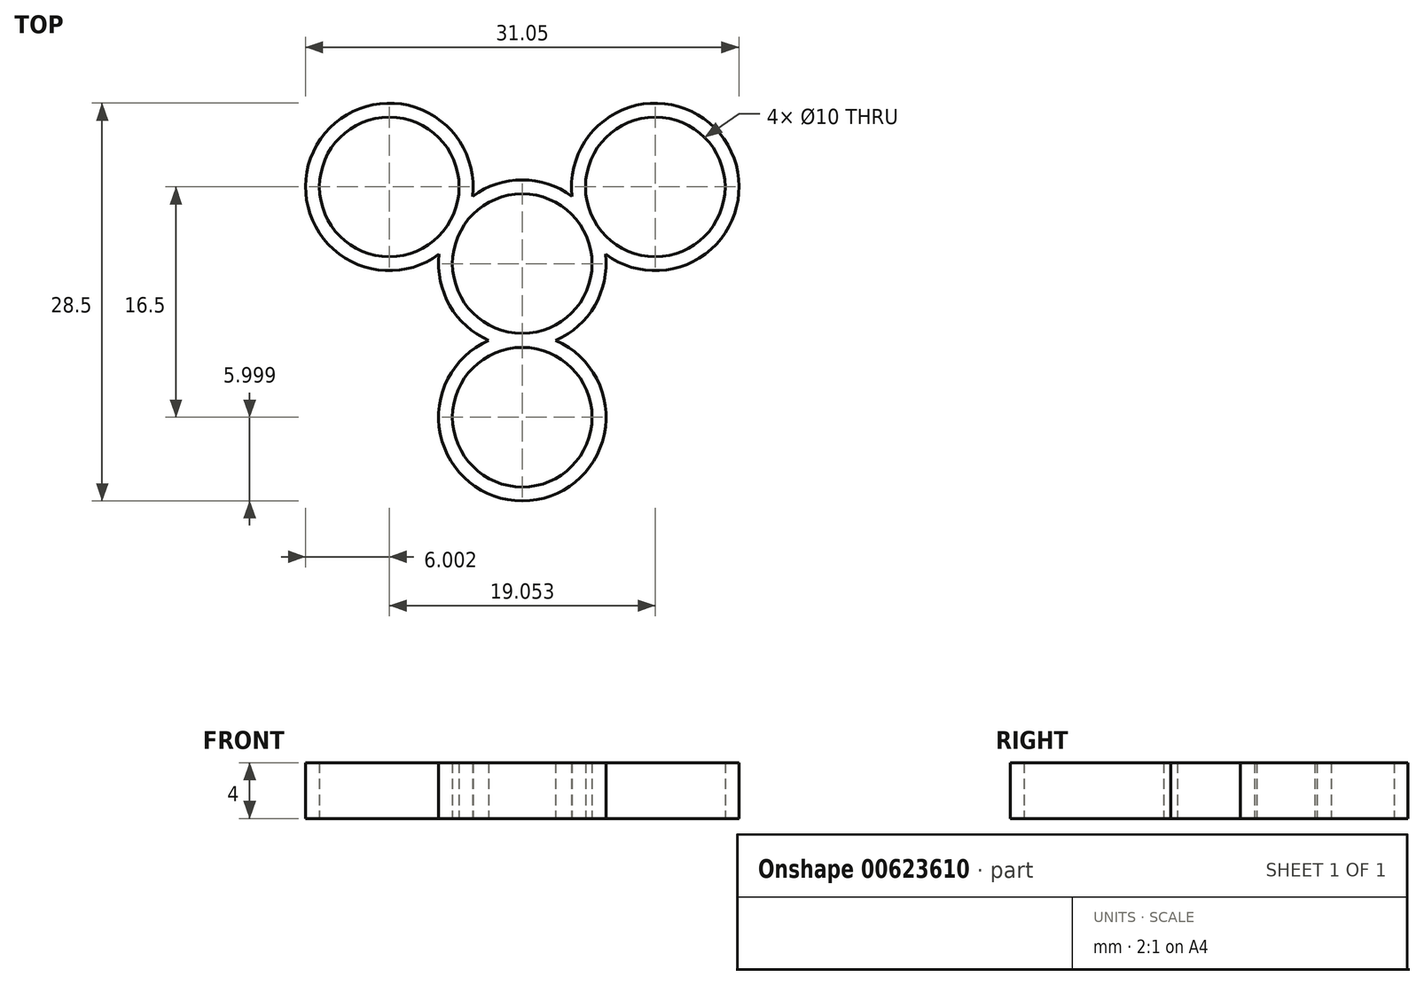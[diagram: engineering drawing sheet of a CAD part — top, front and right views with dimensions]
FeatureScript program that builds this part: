
annotation { "Feature Type Name" : "Feature", "Feature Type Description" : "" }
export const myFeature = defineFeature(function(context is Context, id is Id, definition is map)
    precondition{}
    {
        {
            var Q0;
            Q0=qCreatedBy(makeId("Top.planeOp"),FACE);
            var sketch = newSketch(context, id + "F0", { "sketchPlane" : qUnion([Q0])});
            skCircle(sketch, "E0", {"center": v(-137.71, -10.27) * mm, "radius": 5 * mm});
            skCircle(sketch, "E1", {"center": v(-137.71, -10.27) * mm, "radius": 6 * mm});
            skLineSegment(sketch, "E2", {"start": v(-137.71, -10.27) * mm, "end": v(-137.71, -21.27) * mm});
            skLineSegment(sketch, "E3", {"start": v(-137.71, -10.27) * mm, "end": v(-128.19, -4.77) * mm});
            skLineSegment(sketch, "E4", {"start": v(-137.71, -10.27) * mm, "end": v(-147.24, -4.77) * mm});
            skCircle(sketch, "E5", {"center": v(-128.19, -4.77) * mm, "radius": 5 * mm});
            skCircle(sketch, "E6", {"center": v(-128.19, -4.77) * mm, "radius": 6 * mm});
            skCircle(sketch, "E7", {"center": v(-147.24, -4.77) * mm, "radius": 5 * mm});
            skCircle(sketch, "E8", {"center": v(-147.24, -4.77) * mm, "radius": 6 * mm});
            skCircle(sketch, "E9", {"center": v(-137.71, -21.27) * mm, "radius": 5 * mm});
            skCircle(sketch, "E10", {"center": v(-137.71, -21.27) * mm, "radius": 6 * mm});
            skSolve(sketch);
        }
        {
            var Q0;
            {var subQ0=sQuery(id+"F0.wireOp",EDGE,"E8");var subQ1=sQuery(id+"F0.wireOp",EDGE,"E1");var subQ2=makeQuery(id+"F0.imprint","INTERSECT",VERTEX,{"disambiguationData":[OD(1.0)],"derivedFrom":[subQ1,subQ0]});Q0=makeQuery(id+"F0.imprint","IMPRINT",FACE,{"disambiguationData":[TD([[makeQuery(id+"F0.imprint","IMPRINT",EDGE,{"disambiguationData":[TD([[subQ2,1.0]])],"derivedFrom":subQ1}),1.0]])]});}
            var Q1;
            {var subQ0=sQuery(id+"F0.wireOp",EDGE,"E8");var subQ1=sQuery(id+"F0.wireOp",EDGE,"E1");var subQ2=makeQuery(id+"F0.imprint","INTERSECT",VERTEX,{"disambiguationData":[OD(0.0)],"derivedFrom":[subQ1,subQ0]});Q1=makeQuery(id+"F0.imprint","IMPRINT",FACE,{"disambiguationData":[TD([[makeQuery(id+"F0.imprint","IMPRINT",EDGE,{"disambiguationData":[TD([[subQ2,-1.0]])],"derivedFrom":subQ1}),1.0]])]});}
            var Q2;
            {var subQ3=sQuery(id+"F0.wireOp",EDGE,"E7");Q2=makeQuery(id+"F0.imprint","IMPRINT",FACE,{"disambiguationData":[TD([[makeQuery(id+"F0.imprint","IMPRINT",EDGE,{"derivedFrom":subQ3}),-1.0]])]});}
            var Q3;
            {var subQ0=sQuery(id+"F0.wireOp",EDGE,"E8");var subQ5=sQuery(id+"F0.wireOp",EDGE,"E1");var subQ6=makeQuery(id+"F0.imprint","INTERSECT",VERTEX,{"disambiguationData":[OD(1.0)],"derivedFrom":[subQ5,subQ0]});Q3=makeQuery(id+"F0.imprint","IMPRINT",FACE,{"disambiguationData":[TD([[makeQuery(id+"F0.imprint","IMPRINT",EDGE,{"disambiguationData":[TD([[subQ6,-1.0]])],"derivedFrom":subQ5}),1.0]])]});}
            var Q4;
            {var subQ0=sQuery(id+"F0.wireOp",EDGE,"E6");var subQ5=sQuery(id+"F0.wireOp",EDGE,"E1");var subQ7=makeQuery(id+"F0.imprint","INTERSECT",VERTEX,{"disambiguationData":[OD(0.0)],"derivedFrom":[subQ5,subQ0]});Q4=makeQuery(id+"F0.imprint","IMPRINT",FACE,{"disambiguationData":[TD([[makeQuery(id+"F0.imprint","IMPRINT",EDGE,{"disambiguationData":[TD([[subQ7,1.0]])],"derivedFrom":subQ5}),1.0]])]});}
            var Q5;
            {var subQ3=sQuery(id+"F0.wireOp",EDGE,"E6");var subQ5=sQuery(id+"F0.wireOp",EDGE,"E1");var subQ6=makeQuery(id+"F0.imprint","INTERSECT",VERTEX,{"disambiguationData":[OD(1.0)],"derivedFrom":[subQ5,subQ3]});Q5=makeQuery(id+"F0.imprint","IMPRINT",FACE,{"disambiguationData":[TD([[makeQuery(id+"F0.imprint","IMPRINT",EDGE,{"disambiguationData":[TD([[subQ6,-1.0]])],"derivedFrom":subQ5}),1.0]])]});}
            var Q6;
            {var subQ0=sQuery(id+"F0.wireOp",EDGE,"E10");var subQ1=sQuery(id+"F0.wireOp",EDGE,"E1");var subQ2=makeQuery(id+"F0.imprint","INTERSECT",VERTEX,{"disambiguationData":[OD(1.0)],"derivedFrom":[subQ1,subQ0]});Q6=makeQuery(id+"F0.imprint","IMPRINT",FACE,{"disambiguationData":[TD([[makeQuery(id+"F0.imprint","IMPRINT",EDGE,{"disambiguationData":[TD([[subQ2,1.0]])],"derivedFrom":subQ1}),1.0]])]});}
            var Q7;
            {var subQ0=sQuery(id+"F0.wireOp",EDGE,"E10");var subQ1=sQuery(id+"F0.wireOp",EDGE,"E1");var subQ2=makeQuery(id+"F0.imprint","INTERSECT",VERTEX,{"disambiguationData":[OD(0.0)],"derivedFrom":[subQ1,subQ0]});Q7=makeQuery(id+"F0.imprint","IMPRINT",FACE,{"disambiguationData":[TD([[makeQuery(id+"F0.imprint","IMPRINT",EDGE,{"disambiguationData":[TD([[subQ2,-1.0]])],"derivedFrom":subQ1}),1.0]])]});}
            var Q8;
            {var subQ3=sQuery(id+"F0.wireOp",EDGE,"E9");Q8=makeQuery(id+"F0.imprint","IMPRINT",FACE,{"disambiguationData":[TD([[makeQuery(id+"F0.imprint","IMPRINT",EDGE,{"derivedFrom":subQ3}),-1.0]])]});}
            var Q9;
            {var subQ0=sQuery(id+"F0.wireOp",EDGE,"E6");var subQ1=sQuery(id+"F0.wireOp",EDGE,"E1");var subQ2=makeQuery(id+"F0.imprint","INTERSECT",VERTEX,{"disambiguationData":[OD(0.0)],"derivedFrom":[subQ1,subQ0]});Q9=makeQuery(id+"F0.imprint","IMPRINT",FACE,{"disambiguationData":[TD([[makeQuery(id+"F0.imprint","IMPRINT",EDGE,{"disambiguationData":[TD([[subQ2,-1.0]])],"derivedFrom":subQ1}),1.0]])]});}
            var Q10;
            {var subQ0=sQuery(id+"F0.wireOp",EDGE,"E6");var subQ1=sQuery(id+"F0.wireOp",EDGE,"E1");var subQ2=makeQuery(id+"F0.imprint","INTERSECT",VERTEX,{"disambiguationData":[OD(1.0)],"derivedFrom":[subQ1,subQ0]});Q10=makeQuery(id+"F0.imprint","IMPRINT",FACE,{"disambiguationData":[TD([[makeQuery(id+"F0.imprint","IMPRINT",EDGE,{"disambiguationData":[TD([[subQ2,1.0]])],"derivedFrom":subQ1}),1.0]])]});}
            var Q11;
            {var subQ3=sQuery(id+"F0.wireOp",EDGE,"E5");Q11=makeQuery(id+"F0.imprint","IMPRINT",FACE,{"disambiguationData":[TD([[makeQuery(id+"F0.imprint","IMPRINT",EDGE,{"derivedFrom":subQ3}),-1.0]])]});}
            extrude(context, id + "F1", {"entities" : qUnion([Q0, Q1, Q2, Q3, Q4, Q5, Q6, Q7, Q8, Q9, Q10, Q11]), "depth" : 4 * mm, "offsetDistance" : 25 * mm});
        }
    });
